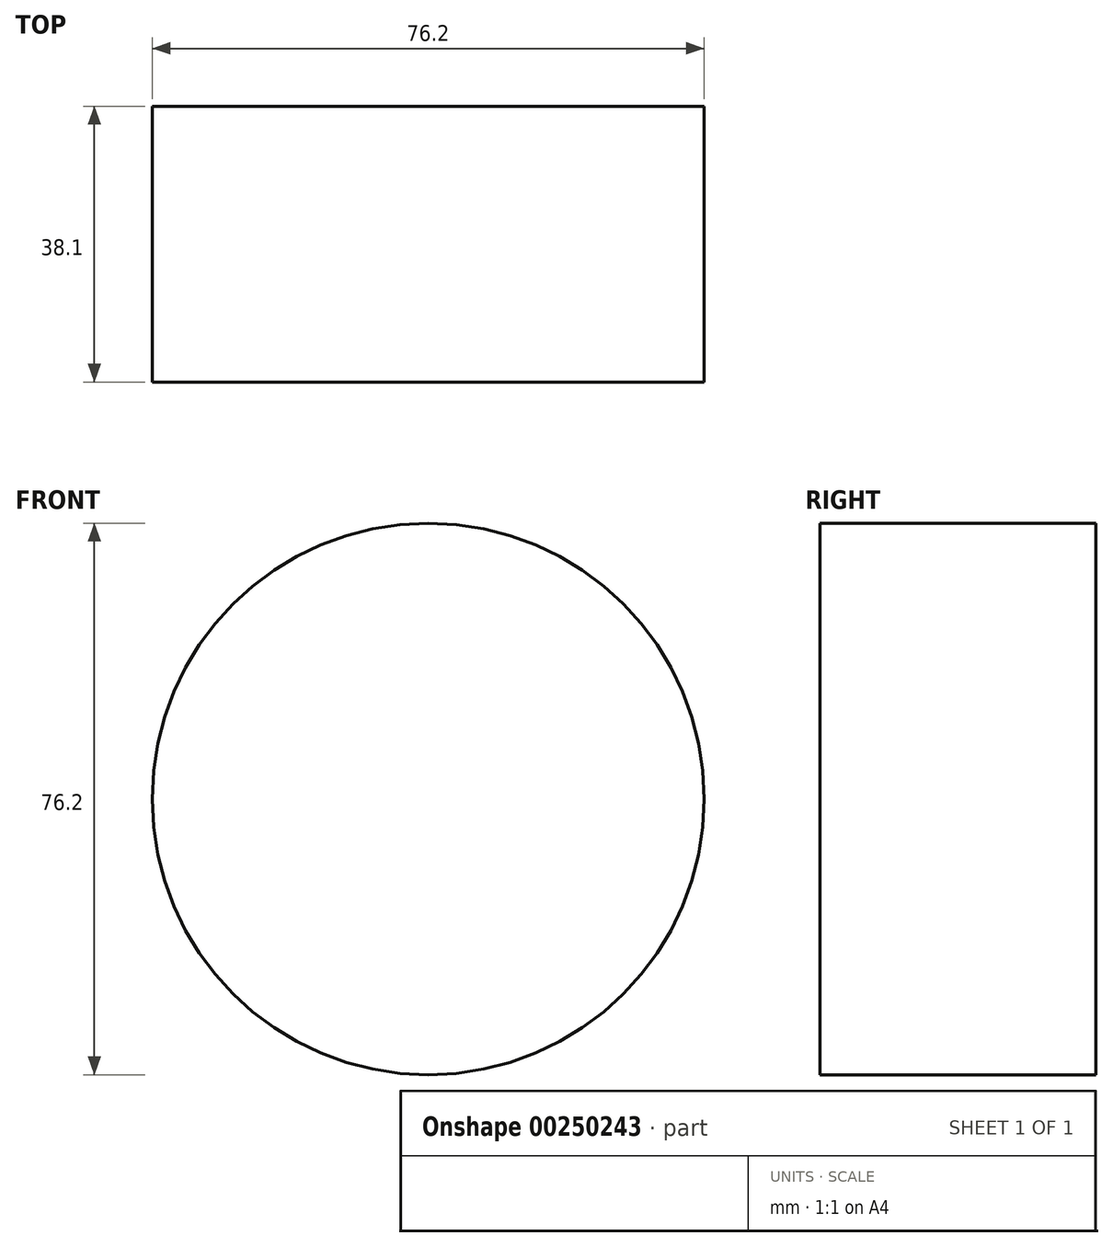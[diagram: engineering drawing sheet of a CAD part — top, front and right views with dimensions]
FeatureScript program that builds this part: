
annotation { "Feature Type Name" : "Feature", "Feature Type Description" : "" }
export const myFeature = defineFeature(function(context is Context, id is Id, definition is map)
    precondition{}
    {
        {
            var Q0;
            Q0=qCreatedBy(makeId("Front.planeOp"),FACE);
            var sketch = newSketch(context, id + "F0", { "sketchPlane" : qUnion([Q0])});
            skCircle(sketch, "E0", {"center": v(0, 0) * mm, "radius": 38.1 * mm});
            skSolve(sketch);
        }
        {
            var Q0;
            Q0 = qSketchRegion(id + "F0", true);
            extrude(context, id + "F1", {"entities" : qUnion([Q0]), "oppositeDirection" : true, "depth" : 38.1 * mm});
        }
    });
